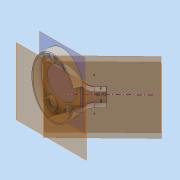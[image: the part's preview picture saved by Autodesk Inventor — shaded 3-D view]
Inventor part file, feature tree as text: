
AUTODESK INVENTOR PART (.ipt)
format: ipt  version: 2019 (Build 230136000, 136)  size: 464,896 bytes
history: native  units: mm
features: other x16, extrude x4, sketch x3, chamfer x1, shell x1, loft x1
ambient origin geometry x8: Origin, YZ Plane, XZ Plane, XY Plane, X Axis, Y Axis, Z Axis, Center Point
bodies: Body1 (feature_tree), Body2 (feature_tree), Body3 (feature_tree)
feature tree (26):
  other  "Твердое тело1"
  other  "Основной эскиз"
  extrude  "Выдавливание1"  Depth=34.31mm
  sketch  "Эскиз7"
  extrude  "Эллипс"  Depth=8.0mm
  other  "РабПлоскость18"
  sketch  "Эскиз19"
  extrude  "Дырки"  Depth=34.31mm
  chamfer  "Фаска для дырок"  Distance=8.0mm
  shell  "Оболочка12"  Thickness=17.93mm
  other  "РабПлоскость33"
  other  "РабПлоскость34"
  sketch  "Эскиз26"
  extrude  "Выдавливание23"  Depth=25.93mm
  loft  "Лофт7"
  other  "Удаление грани5"
  other  "Удаление грани6"
  other  "Удаление грани7"
  other  "Удаление грани8"
  other  "Удаление грани9"
  other  "Удаление грани10"
  other  "Удаление грани11"
  other  "Твердое тело7"
  other  "Твердое тело13"
  other  "Ребра12"
  other  "Ребра13"
